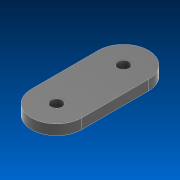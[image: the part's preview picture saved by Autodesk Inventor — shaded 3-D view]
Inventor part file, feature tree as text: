
AUTODESK INVENTOR PART (.ipt)
format: ipt  version: 2022.2 (Build 262287000, 287)  size: 93,696 bytes
history: native  units: in
note: dims shown in document units (in); Inventor stores cm internally (conversion verified against a paired STEP export)
features: extrude x1, sketch x1
ambient origin geometry x8: Origin, YZ Plane, XZ Plane, XY Plane, X Axis, Y Axis, Z Axis, Center Point
bodies: Solid1 (feature_tree)
feature tree (2):
  extrude  "Extrusion1"  Depth=1.0in
  sketch  "Sketch1"  dims[d0=0.17in d2=1.0in d3=0.75in d4=0.152in d5=0.0in]
